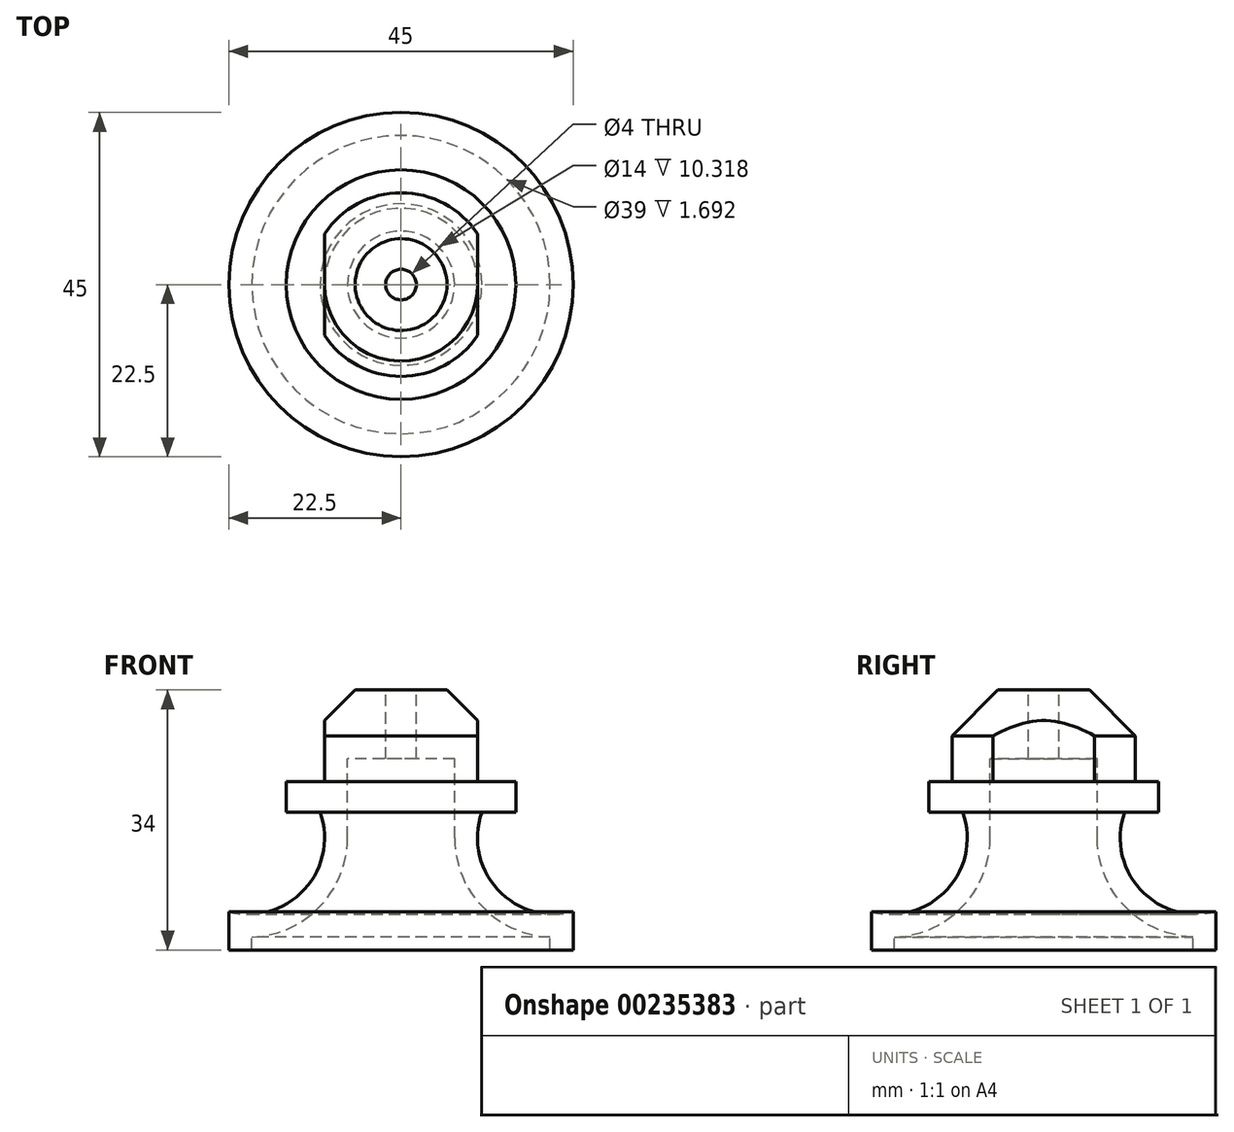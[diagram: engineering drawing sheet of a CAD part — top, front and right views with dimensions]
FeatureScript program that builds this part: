
annotation { "Feature Type Name" : "Feature", "Feature Type Description" : "" }
export const myFeature = defineFeature(function(context is Context, id is Id, definition is map)
    precondition{}
    {
        {
            var Q0;
            Q0=qCreatedBy(makeId("Front.planeOp"),FACE);
            var sketch = newSketch(context, id + "F0", { "sketchPlane" : qUnion([Q0])});
            skLineSegment(sketch, "E0", {"start": v(0, 0) * mm, "end": v(22.5, 0) * mm});
            skLineSegment(sketch, "E1", {"start": v(22.5, 5) * mm, "end": v(22.5, 0) * mm});
            skLineSegment(sketch, "E2", {"start": v(0, 0) * mm, "end": v(0, 34) * mm});
            skLineSegment(sketch, "E3", {"start": v(2, 34) * mm, "end": v(0, 34) * mm});
            skLineSegment(sketch, "E4", {"start": v(2, 34) * mm, "end": v(2, 25) * mm});
            skLineSegment(sketch, "E5", {"start": v(2, 25) * mm, "end": v(0, 25) * mm});
            skLineSegment(sketch, "E6", {"start": v(2, 25) * mm, "end": v(7, 25) * mm});
            skLineSegment(sketch, "E7", {"start": v(7, 25) * mm, "end": v(7, 14.68) * mm});
            skLineSegment(sketch, "E8", {"start": v(2, 34) * mm, "end": v(6, 34) * mm});
            skLineSegment(sketch, "E9", {"start": v(6, 34) * mm, "end": v(42.1, 34) * mm});
            skLineSegment(sketch, "E10", {"start": v(6, 34) * mm, "end": v(12, 28) * mm});
            skLineSegment(sketch, "E11", {"start": v(12, 28) * mm, "end": v(12, 22) * mm});
            skLineSegment(sketch, "E12", {"start": v(12, 22) * mm, "end": v(15, 22) * mm});
            skLineSegment(sketch, "E13", {"start": v(15, 22) * mm, "end": v(15, 18) * mm});
            skLineSegment(sketch, "E14", {"start": v(15, 18) * mm, "end": v(10.57, 18) * mm});
            skArc(sketch, "E15", {"start": v(10.57, 18) * mm, "mid": v(12.63, 7.92) * mm, "end": v(22.5, 5) * mm});
            skArc(sketch, "E16.0", {"start": v(7, 14.68) * mm, "mid": v(10.63, 5.67) * mm, "end": v(19.5, 1.7) * mm});
            skLineSegment(sketch, "E17", {"start": v(19.5, 1.7) * mm, "end": v(19.5, 0) * mm});
            skLineSegment(sketch, "E18", {"start": v(19.5, 0) * mm, "end": v(22.5, 0) * mm});
            skLineSegment(sketch, "E19", {"start": v(0, 67.47) * mm, "end": v(0, -52.41) * mm});
            skSolve(sketch);
        }
        {
            var Q0;
            Q0=makeQuery(id+"F0.imprint","IMPRINT",FACE,{"disambiguationData":[TD([[makeQuery(id+"F0.imprint","IMPRINT",EDGE,{"derivedFrom":sQuery(id+"F0.wireOp",EDGE,"E1")}),-1.0]])]});
            var Q1;
            Q1=sQuery(id+"F0.wireOp",EDGE,"E19");
            revolve(context, id + "F1", {"entities" : qUnion([Q0]), "axis" : qUnion([Q1]), "revolveType" : RevolveType.FULL});
        }
        {
            var Q0;
            Q0=makeQuery(id+"F1.opRevolve","SWEPT_FACE",FACE,{"disambiguationData":[OSD([sQuery(id+"F0.wireOp",EDGE,"E8")])]});
            var sketch = newSketch(context, id + "F2", { "sketchPlane" : qUnion([Q0])});
            skLineSegment(sketch, "E20.bottom", {"start": v(10, -6.63) * mm, "end": v(-10, -6.63) * mm});
            skLineSegment(sketch, "E20.top", {"start": v(10, 6.63) * mm, "end": v(-10, 6.63) * mm});
            skLineSegment(sketch, "E20.left", {"start": v(10, -6.63) * mm, "end": v(10, 6.63) * mm});
            skLineSegment(sketch, "E20.right", {"start": v(-10, -6.63) * mm, "end": v(-10, 6.63) * mm});
            skPoint(sketch, "E20.middle", {"position": v(0, 0) * mm});
            skCircle(sketch, "E21", {"center": v(0, 0) * mm, "radius": 12 * mm});
            skSolve(sketch);
        }
        {
            var Q0;
            {var subQ0=sQuery(id+"F2.wireOp",EDGE,"E20.left");Q0=makeQuery(id+"F2.imprint","IMPRINT",FACE,{"disambiguationData":[TD([[makeQuery(id+"F2.imprint","IMPRINT",EDGE,{"derivedFrom":subQ0}),-1.0]])]});}
            var Q1;
            {var subQ0=sQuery(id+"F2.wireOp",EDGE,"E20.right");Q1=makeQuery(id+"F2.imprint","IMPRINT",FACE,{"disambiguationData":[TD([[makeQuery(id+"F2.imprint","IMPRINT",EDGE,{"derivedFrom":subQ0}),1.0]])]});}
            var Q2;
            Q2=makeQuery(id+"F1.opRevolve","SWEPT_FACE",FACE,{"disambiguationData":[OSD([sQuery(id+"F0.wireOp",EDGE,"E12")])]});
            extrude(context, id + "F3", {"entities" : qUnion([Q0, Q1]), "operationType" : NewBodyOperationType.REMOVE, "endBound" : BoundingType.UP_TO_SURFACE, "oppositeDirection" : true, "endBoundEntityFace" : qUnion([Q2]), "depth" : 25 * mm});
        }
    });
